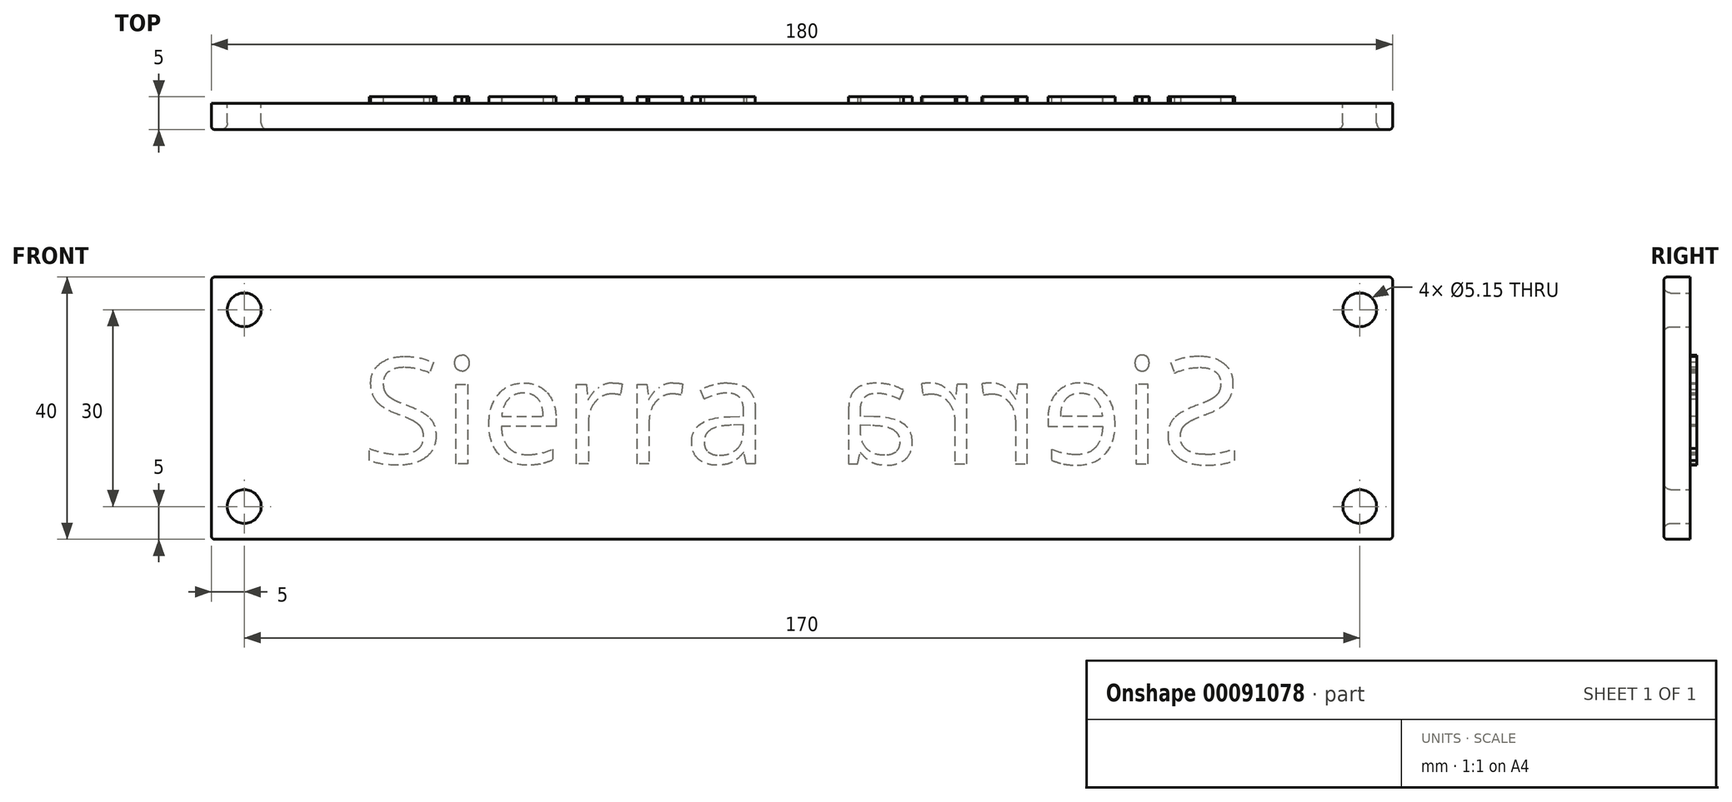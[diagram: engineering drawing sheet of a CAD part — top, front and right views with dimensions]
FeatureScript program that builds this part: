
annotation { "Feature Type Name" : "Feature", "Feature Type Description" : "" }
export const myFeature = defineFeature(function(context is Context, id is Id, definition is map)
    precondition{}
    {
        {
            var Q0;
            Q0=qCreatedBy(makeId("Front.planeOp"),FACE);
            var sketch = newSketch(context, id + "F0", { "sketchPlane" : qUnion([Q0])});
            skLineSegment(sketch, "E0.bottom", {"start": v(-90, -20) * mm, "end": v(90, -20) * mm});
            skLineSegment(sketch, "E0.top", {"start": v(-90, 20) * mm, "end": v(90, 20) * mm});
            skLineSegment(sketch, "E0.left", {"start": v(-90, -20) * mm, "end": v(-90, 20) * mm});
            skLineSegment(sketch, "E0.right", {"start": v(90, -20) * mm, "end": v(90, 20) * mm});
            skPoint(sketch, "E0.middle", {"position": v(0, 0) * mm});
            skCircle(sketch, "E1", {"center": v(-85, 15) * mm, "radius": 2.58 * mm});
            skPoint(sketch, "E2.start.orphan", {"position": v(-90, 0) * mm});
            skPoint(sketch, "E3.orphan", {"position": v(0, 20) * mm});
            skPoint(sketch, "E4.end.orphan", {"position": v(0, -20) * mm});
            skLineSegment(sketch, "E5", {"start": v(-90, 0) * mm, "end": v(0, 0) * mm, "construction": true});
            skLineSegment(sketch, "E6", {"start": v(0, 20) * mm, "end": v(0, -20) * mm, "construction": true});
            skCircle(sketch, "E7.MirrorC", {"center": v(-85, -15) * mm, "radius": 2.58 * mm});
            skCircle(sketch, "E8.MirrorC", {"center": v(85, 15) * mm, "radius": 2.58 * mm});
            skCircle(sketch, "E9.MirrorC", {"center": v(85, -15) * mm, "radius": 2.58 * mm});
            skSolve(sketch);
        }
        {
            var Q0;
            Q0=makeQuery(id+"F0.imprint","IMPRINT",FACE,{"disambiguationData":[TD([[makeQuery(id+"F0.imprint","IMPRINT",EDGE,{"derivedFrom":sQuery(id+"F0.wireOp",EDGE,"E0.bottom")}),1.0]])]});
            extrude(context, id + "F1", {"entities" : qUnion([Q0]), "depth" : 4 * mm});
        }
        {
            var Q0;
            Q0=makeQuery(id+"F1.opExtrude","CAP_EDGE",EDGE,{"disambiguationData":[OSD([sQuery(id+"F0.wireOp",EDGE,"E1")])],"isStart":false});
            var Q1;
            Q1=makeQuery(id+"F1.opExtrude","CAP_EDGE",EDGE,{"disambiguationData":[OSD([sQuery(id+"F0.wireOp",EDGE,"f5b72a5b-8583-449a-bdbf-9ac5a681e1fd0.MirrorC")])],"isStart":false});
            var Q2;
            Q2=makeQuery(id+"F1.opExtrude","CAP_EDGE",EDGE,{"disambiguationData":[OSD([sQuery(id+"F0.wireOp",EDGE,"2623e306-60f4-4522-aa65-1e3e8c2cf5b60.MirrorC")])],"isStart":false});
            var Q3;
            Q3=makeQuery(id+"F1.opExtrude","CAP_EDGE",EDGE,{"disambiguationData":[OSD([sQuery(id+"F0.wireOp",EDGE,"be81a34d-1d50-4ce7-a7a8-4484a1701fac0.MirrorC")])],"isStart":false});
            var Q4;
            Q4=makeQuery(id+"F1.opExtrude","CAP_EDGE",EDGE,{"disambiguationData":[OSD([sQuery(id+"F0.wireOp",EDGE,"E7.MirrorC")])],"isStart":false});
            var Q5;
            Q5=makeQuery(id+"F1.opExtrude","CAP_EDGE",EDGE,{"disambiguationData":[OSD([sQuery(id+"F0.wireOp",EDGE,"E8.MirrorC")])],"isStart":false});
            var Q6;
            Q6=makeQuery(id+"F1.opExtrude","CAP_EDGE",EDGE,{"disambiguationData":[OSD([sQuery(id+"F0.wireOp",EDGE,"E9.MirrorC")])],"isStart":false});
            fillet(context, id + "F2", {"entities" : qUnion([Q0, Q1, Q2, Q3, Q4, Q5, Q6]), "radius" : 1 * mm, "tangentPropagation" : true, "allowEdgeOverflow" : false});
        }
        {
            var Q0;
            Q0=makeQuery(id+"F1.opExtrude","CAP_EDGE",EDGE,{"disambiguationData":[OSD([sQuery(id+"F0.wireOp",EDGE,"E0.top")])],"isStart":false});
            var Q1;
            Q1=makeQuery(id+"F1.opExtrude","CAP_EDGE",EDGE,{"disambiguationData":[OSD([sQuery(id+"F0.wireOp",EDGE,"E0.left")])],"isStart":false});
            var Q2;
            Q2=makeQuery(id+"F1.opExtrude","CAP_EDGE",EDGE,{"disambiguationData":[OSD([sQuery(id+"F0.wireOp",EDGE,"E0.bottom")])],"isStart":false});
            var Q3;
            Q3=makeQuery(id+"F1.opExtrude","CAP_EDGE",EDGE,{"disambiguationData":[OSD([sQuery(id+"F0.wireOp",EDGE,"E0.right")])],"isStart":false});
            var Q4;
            Q4=makeQuery(id+"F1.opExtrude","SWEPT_EDGE",EDGE,{"disambiguationData":[OSD([sQuery(id+"F0.wireOp",EDGE,"E0.top"),sQuery(id+"F0.wireOp",EDGE,"E0.left")])]});
            var Q5;
            Q5=makeQuery(id+"F1.opExtrude","SWEPT_EDGE",EDGE,{"disambiguationData":[OSD([sQuery(id+"F0.wireOp",EDGE,"E0.bottom"),sQuery(id+"F0.wireOp",EDGE,"E0.left")])]});
            var Q6;
            Q6=makeQuery(id+"F1.opExtrude","SWEPT_EDGE",EDGE,{"disambiguationData":[OSD([sQuery(id+"F0.wireOp",EDGE,"E0.top"),sQuery(id+"F0.wireOp",EDGE,"E0.right")])]});
            var Q7;
            Q7=makeQuery(id+"F1.opExtrude","SWEPT_EDGE",EDGE,{"disambiguationData":[OSD([sQuery(id+"F0.wireOp",EDGE,"E0.bottom"),sQuery(id+"F0.wireOp",EDGE,"E0.right")])]});
            fillet(context, id + "F3", {"entities" : qUnion([Q0, Q1, Q2, Q3, Q4, Q5, Q6, Q7]), "radius" : .5 * mm, "tangentPropagation" : true, "allowEdgeOverflow" : false});
        }
        {
            var Q0;
            Q0=makeQuery(id+"F1.opExtrude","CAP_FACE",FACE,{"disambiguationData":[OSD([sQuery(id+"F0.wireOp",EDGE,"E0.bottom"),sQuery(id+"F0.wireOp",EDGE,"E0.top"),sQuery(id+"F0.wireOp",EDGE,"E0.left"),sQuery(id+"F0.wireOp",EDGE,"E0.right"),sQuery(id+"F0.wireOp",EDGE,"E1"),sQuery(id+"F0.wireOp",EDGE,"E7.MirrorC"),sQuery(id+"F0.wireOp",EDGE,"E8.MirrorC"),sQuery(id+"F0.wireOp",EDGE,"E9.MirrorC")])],"isStart":true});
            var sketch = newSketch(context, id + "F4", { "sketchPlane" : qUnion([Q0])});
            skText(sketch, "E10", { "text": "Sierra\n", "fontName": "OpenSans-Regular.ttf"});
            skLineSegment(sketch, "E11", {"start": v(0, 20) * mm, "end": v(0, -20) * mm, "construction": true});
            const initialGuessF4  = {"E10": [-0.0671, -0.00847, 1, 0, 0.01627]};
            skSetInitialGuess(sketch, initialGuessF4);
            skSolve(sketch);
        }
        {
            var Q0;
            Q0=qSketchRegion(id+"F4",true);
            extrude(context, id + "F5", {"entities" : qUnion([Q0]), "operationType" : NewBodyOperationType.ADD, "depth" : 1 * mm});
        }
        {
            var Q0;
            Q0=makeQuery(id+"F1.opExtrude","SWEPT_BODY",BODY,{"disambiguationData":[OSD([sQuery(id+"F0.wireOp",EDGE,"E0.bottom"),sQuery(id+"F0.wireOp",EDGE,"E0.top"),sQuery(id+"F0.wireOp",EDGE,"E0.left"),sQuery(id+"F0.wireOp",EDGE,"E0.right"),sQuery(id+"F0.wireOp",EDGE,"E1"),sQuery(id+"F0.wireOp",EDGE,"E7.MirrorC"),sQuery(id+"F0.wireOp",EDGE,"E8.MirrorC"),sQuery(id+"F0.wireOp",EDGE,"E9.MirrorC")])]});
            var Q1;
            Q1=makeQuery(id+"F5.opExtrude","SWEPT_FACE",FACE,{"disambiguationData":[OSD([sQuery(id+"F4.wireOp",EDGE,"E10.sketch_text.stroke-94")])]});
            var Q2;
            Q2=makeQuery(id+"F5.opExtrude","SWEPT_FACE",FACE,{"disambiguationData":[OSD([sQuery(id+"F4.wireOp",EDGE,"E10.sketch_text.stroke-169")])]});
            var Q3;
            Q3=makeQuery(id+"F5.opExtrude","SWEPT_FACE",FACE,{"disambiguationData":[OSD([sQuery(id+"F4.wireOp",EDGE,"E10.sketch_text.stroke-185")])]});
            var Q4;
            Q4=makeQuery(id+"F5.opExtrude","SWEPT_FACE",FACE,{"disambiguationData":[OSD([sQuery(id+"F4.wireOp",EDGE,"E10.sketch_text.stroke-125")])]});
            var Q5;
            Q5=makeQuery(id+"F5.opExtrude","SWEPT_FACE",FACE,{"disambiguationData":[OSD([sQuery(id+"F4.wireOp",EDGE,"E10.sketch_text.stroke-155")])]});
            var Q6;
            Q6=makeQuery(id+"F5.opExtrude","SWEPT_FACE",FACE,{"disambiguationData":[OSD([sQuery(id+"F4.wireOp",EDGE,"E10.sketch_text.stroke-65")])]});
            var Q7;
            Q7=makeQuery(id+"F5.opExtrude","SWEPT_FACE",FACE,{"disambiguationData":[OSD([sQuery(id+"F4.wireOp",EDGE,"E10.sketch_text.stroke-81")])]});
            var Q8;
            Q8=makeQuery(id+"F5.opExtrude","SWEPT_FACE",FACE,{"disambiguationData":[OSD([sQuery(id+"F4.wireOp",EDGE,"E10.sketch_text.stroke-67")])]});
            var Q9;
            Q9=makeQuery(id+"F5.opExtrude","SWEPT_FACE",FACE,{"disambiguationData":[OSD([sQuery(id+"F4.wireOp",EDGE,"E10.sketch_text.stroke-99")])]});
            var Q10;
            Q10=makeQuery(id+"F5.opExtrude","SWEPT_FACE",FACE,{"disambiguationData":[OSD([sQuery(id+"F4.wireOp",EDGE,"E10.sketch_text.stroke-127")])]});
            var Q11;
            Q11=makeQuery(id+"F5.opExtrude","SWEPT_FACE",FACE,{"disambiguationData":[OSD([sQuery(id+"F4.wireOp",EDGE,"E10.sketch_text.stroke-10")])]});
            var Q12;
            Q12=makeQuery(id+"F5.opExtrude","CAP_FACE",FACE,{"disambiguationData":[OSD([sQuery(id+"F4.wireOp",EDGE,"E10.sketch_text.stroke-9"),sQuery(id+"F4.wireOp",EDGE,"E10.sketch_text.stroke-10"),sQuery(id+"F4.wireOp",EDGE,"E10.sketch_text.stroke-11"),sQuery(id+"F4.wireOp",EDGE,"E10.sketch_text.stroke-12")])],"isStart":false});
            var Q13;
            Q13=makeQuery(id+"F5.opExtrude","SWEPT_FACE",FACE,{"disambiguationData":[OSD([sQuery(id+"F4.wireOp",EDGE,"E10.sketch_text.stroke-154")])]});
            var Q14;
            Q14=makeQuery(id+"F5.opExtrude","SWEPT_FACE",FACE,{"disambiguationData":[OSD([sQuery(id+"F4.wireOp",EDGE,"E10.sketch_text.stroke-1")])]});
            var Q15;
            Q15=makeQuery(id+"F5.opExtrude","CAP_FACE",FACE,{"disambiguationData":[OSD([sQuery(id+"F4.wireOp",EDGE,"E10.sketch_text.stroke-124"),sQuery(id+"F4.wireOp",EDGE,"E10.sketch_text.stroke-125"),sQuery(id+"F4.wireOp",EDGE,"E10.sketch_text.stroke-126"),sQuery(id+"F4.wireOp",EDGE,"E10.sketch_text.stroke-127"),sQuery(id+"F4.wireOp",EDGE,"E10.sketch_text.stroke-128"),sQuery(id+"F4.wireOp",EDGE,"E10.sketch_text.stroke-129"),sQuery(id+"F4.wireOp",EDGE,"E10.sketch_text.stroke-130"),sQuery(id+"F4.wireOp",EDGE,"E10.sketch_text.stroke-131"),sQuery(id+"F4.wireOp",EDGE,"E10.sketch_text.stroke-132"),sQuery(id+"F4.wireOp",EDGE,"E10.sketch_text.stroke-133"),sQuery(id+"F4.wireOp",EDGE,"E10.sketch_text.stroke-134"),sQuery(id+"F4.wireOp",EDGE,"E10.sketch_text.stroke-135"),sQuery(id+"F4.wireOp",EDGE,"E10.sketch_text.stroke-136"),sQuery(id+"F4.wireOp",EDGE,"E10.sketch_text.stroke-137"),sQuery(id+"F4.wireOp",EDGE,"E10.sketch_text.stroke-138")])],"isStart":false});
            var Q16;
            Q16=makeQuery(id+"F5.opExtrude","CAP_FACE",FACE,{"disambiguationData":[OSD([sQuery(id+"F4.wireOp",EDGE,"E10.sketch_text.stroke-34"),sQuery(id+"F4.wireOp",EDGE,"E10.sketch_text.stroke-35"),sQuery(id+"F4.wireOp",EDGE,"E10.sketch_text.stroke-36"),sQuery(id+"F4.wireOp",EDGE,"E10.sketch_text.stroke-37"),sQuery(id+"F4.wireOp",EDGE,"E10.sketch_text.stroke-38"),sQuery(id+"F4.wireOp",EDGE,"E10.sketch_text.stroke-39"),sQuery(id+"F4.wireOp",EDGE,"E10.sketch_text.stroke-40"),sQuery(id+"F4.wireOp",EDGE,"E10.sketch_text.stroke-41"),sQuery(id+"F4.wireOp",EDGE,"E10.sketch_text.stroke-42"),sQuery(id+"F4.wireOp",EDGE,"E10.sketch_text.stroke-43"),sQuery(id+"F4.wireOp",EDGE,"E10.sketch_text.stroke-44"),sQuery(id+"F4.wireOp",EDGE,"E10.sketch_text.stroke-45"),sQuery(id+"F4.wireOp",EDGE,"E10.sketch_text.stroke-46"),sQuery(id+"F4.wireOp",EDGE,"E10.sketch_text.stroke-47"),sQuery(id+"F4.wireOp",EDGE,"E10.sketch_text.stroke-48"),sQuery(id+"F4.wireOp",EDGE,"E10.sketch_text.stroke-49"),sQuery(id+"F4.wireOp",EDGE,"E10.sketch_text.stroke-50"),sQuery(id+"F4.wireOp",EDGE,"E10.sketch_text.stroke-51"),sQuery(id+"F4.wireOp",EDGE,"E10.sketch_text.stroke-52"),sQuery(id+"F4.wireOp",EDGE,"E10.sketch_text.stroke-53"),sQuery(id+"F4.wireOp",EDGE,"E10.sketch_text.stroke-54"),sQuery(id+"F4.wireOp",EDGE,"E10.sketch_text.stroke-55"),sQuery(id+"F4.wireOp",EDGE,"E10.sketch_text.stroke-56"),sQuery(id+"F4.wireOp",EDGE,"E10.sketch_text.stroke-57"),sQuery(id+"F4.wireOp",EDGE,"E10.sketch_text.stroke-58"),sQuery(id+"F4.wireOp",EDGE,"E10.sketch_text.stroke-59"),sQuery(id+"F4.wireOp",EDGE,"E10.sketch_text.stroke-60")])],"isStart":false});
            var Q17;
            Q17=makeQuery(id+"F5.opExtrude","SWEPT_FACE",FACE,{"disambiguationData":[OSD([sQuery(id+"F4.wireOp",EDGE,"E10.sketch_text.stroke-50")])]});
            var Q18;
            Q18=makeQuery(id+"F5.opExtrude","SWEPT_FACE",FACE,{"disambiguationData":[OSD([sQuery(id+"F4.wireOp",EDGE,"E10.sketch_text.stroke-2")])]});
            var Q19;
            Q19=makeQuery(id+"F5.opExtrude","SWEPT_FACE",FACE,{"disambiguationData":[OSD([sQuery(id+"F4.wireOp",EDGE,"E10.sketch_text.stroke-3")])]});
            var Q20;
            Q20=makeQuery(id+"F5.opExtrude","SWEPT_FACE",FACE,{"disambiguationData":[OSD([sQuery(id+"F4.wireOp",EDGE,"E10.sketch_text.stroke-5")])]});
            var Q21;
            Q21=makeQuery(id+"F5.opExtrude","SWEPT_FACE",FACE,{"disambiguationData":[OSD([sQuery(id+"F4.wireOp",EDGE,"E10.sketch_text.stroke-8")])]});
            var Q22;
            Q22=makeQuery(id+"F5.opExtrude","SWEPT_FACE",FACE,{"disambiguationData":[OSD([sQuery(id+"F4.wireOp",EDGE,"E10.sketch_text.stroke-98")])]});
            var Q23;
            Q23=makeQuery(id+"F5.opExtrude","SWEPT_FACE",FACE,{"disambiguationData":[OSD([sQuery(id+"F4.wireOp",EDGE,"E10.sketch_text.stroke-66")])]});
            var Q24;
            Q24=makeQuery(id+"F5.opExtrude","SWEPT_FACE",FACE,{"disambiguationData":[OSD([sQuery(id+"F4.wireOp",EDGE,"E10.sketch_text.stroke-153")])]});
            var Q25;
            Q25=makeQuery(id+"F5.opExtrude","SWEPT_FACE",FACE,{"disambiguationData":[OSD([sQuery(id+"F4.wireOp",EDGE,"E10.sketch_text.stroke-126")])]});
            var Q26;
            Q26=makeQuery(id+"F5.opExtrude","SWEPT_FACE",FACE,{"disambiguationData":[OSD([sQuery(id+"F4.wireOp",EDGE,"E10.sketch_text.stroke-183")])]});
            var Q27;
            Q27=makeQuery(id+"F5.opExtrude","SWEPT_FACE",FACE,{"disambiguationData":[OSD([sQuery(id+"F4.wireOp",EDGE,"E10.sketch_text.stroke-109")])]});
            var Q28;
            Q28=makeQuery(id+"F5.opExtrude","SWEPT_FACE",FACE,{"disambiguationData":[OSD([sQuery(id+"F4.wireOp",EDGE,"E10.sketch_text.stroke-186")])]});
            var Q29;
            Q29=makeQuery(id+"F5.opExtrude","SWEPT_FACE",FACE,{"disambiguationData":[OSD([sQuery(id+"F4.wireOp",EDGE,"E10.sketch_text.stroke-79")])]});
            var Q30;
            Q30=makeQuery(id+"F5.opExtrude","SWEPT_FACE",FACE,{"disambiguationData":[OSD([sQuery(id+"F4.wireOp",EDGE,"E10.sketch_text.stroke-110")])]});
            var Q31;
            Q31=makeQuery(id+"F5.opExtrude","SWEPT_FACE",FACE,{"disambiguationData":[OSD([sQuery(id+"F4.wireOp",EDGE,"E10.sketch_text.stroke-38")])]});
            var Q32;
            Q32=makeQuery(id+"F5.opExtrude","SWEPT_FACE",FACE,{"disambiguationData":[OSD([sQuery(id+"F4.wireOp",EDGE,"E10.sketch_text.stroke-24")])]});
            var Q33;
            Q33=makeQuery(id+"F5.opExtrude","SWEPT_FACE",FACE,{"disambiguationData":[OSD([sQuery(id+"F4.wireOp",EDGE,"E10.sketch_text.stroke-12")])]});
            var Q34;
            Q34=makeQuery(id+"F5.opExtrude","SWEPT_FACE",FACE,{"disambiguationData":[OSD([sQuery(id+"F4.wireOp",EDGE,"E10.sketch_text.stroke-100")])]});
            var Q35;
            Q35=makeQuery(id+"F5.opExtrude","SWEPT_FACE",FACE,{"disambiguationData":[OSD([sQuery(id+"F4.wireOp",EDGE,"E10.sketch_text.stroke-158")])]});
            var Q36;
            Q36=makeQuery(id+"F5.opExtrude","SWEPT_FACE",FACE,{"disambiguationData":[OSD([sQuery(id+"F4.wireOp",EDGE,"E10.sketch_text.stroke-142")])]});
            var Q37;
            Q37=makeQuery(id+"F5.opExtrude","SWEPT_FACE",FACE,{"disambiguationData":[OSD([sQuery(id+"F4.wireOp",EDGE,"E10.sketch_text.stroke-54")])]});
            var Q38;
            Q38=makeQuery(id+"F5.opExtrude","SWEPT_FACE",FACE,{"disambiguationData":[OSD([sQuery(id+"F4.wireOp",EDGE,"E10.sketch_text.stroke-25")])]});
            var Q39;
            Q39=makeQuery(id+"F5.opExtrude","SWEPT_FACE",FACE,{"disambiguationData":[OSD([sQuery(id+"F4.wireOp",EDGE,"E10.sketch_text.stroke-101")])]});
            var Q40;
            Q40=makeQuery(id+"F5.opExtrude","SWEPT_FACE",FACE,{"disambiguationData":[OSD([sQuery(id+"F4.wireOp",EDGE,"E10.sketch_text.stroke-69")])]});
            var Q41;
            Q41=makeQuery(id+"F5.opExtrude","SWEPT_FACE",FACE,{"disambiguationData":[OSD([sQuery(id+"F4.wireOp",EDGE,"E10.sketch_text.stroke-159")])]});
            var Q42;
            Q42=makeQuery(id+"F5.opExtrude","SWEPT_FACE",FACE,{"disambiguationData":[OSD([sQuery(id+"F4.wireOp",EDGE,"E10.sketch_text.stroke-85")])]});
            var Q43;
            Q43=makeQuery(id+"F5.opExtrude","SWEPT_FACE",FACE,{"disambiguationData":[OSD([sQuery(id+"F4.wireOp",EDGE,"E10.sketch_text.stroke-173")])]});
            var Q44;
            Q44=makeQuery(id+"F5.opExtrude","SWEPT_FACE",FACE,{"disambiguationData":[OSD([sQuery(id+"F4.wireOp",EDGE,"E10.sketch_text.stroke-40")])]});
            var Q45;
            Q45=makeQuery(id+"F5.opExtrude","SWEPT_FACE",FACE,{"disambiguationData":[OSD([sQuery(id+"F4.wireOp",EDGE,"E10.sketch_text.stroke-102")])]});
            var Q46;
            Q46=makeQuery(id+"F5.opExtrude","SWEPT_FACE",FACE,{"disambiguationData":[OSD([sQuery(id+"F4.wireOp",EDGE,"E10.sketch_text.stroke-86")])]});
            var Q47;
            Q47=makeQuery(id+"F5.opExtrude","SWEPT_FACE",FACE,{"disambiguationData":[OSD([sQuery(id+"F4.wireOp",EDGE,"E10.sketch_text.stroke-130")])]});
            var Q48;
            Q48=makeQuery(id+"F5.opExtrude","SWEPT_FACE",FACE,{"disambiguationData":[OSD([sQuery(id+"F4.wireOp",EDGE,"E10.sketch_text.stroke-103")])]});
            var Q49;
            Q49=makeQuery(id+"F5.opExtrude","SWEPT_FACE",FACE,{"disambiguationData":[OSD([sQuery(id+"F4.wireOp",EDGE,"E10.sketch_text.stroke-87")])]});
            var Q50;
            Q50=makeQuery(id+"F5.opExtrude","SWEPT_FACE",FACE,{"disambiguationData":[OSD([sQuery(id+"F4.wireOp",EDGE,"E10.sketch_text.stroke-145")])]});
            var Q51;
            Q51=makeQuery(id+"F5.opExtrude","SWEPT_FACE",FACE,{"disambiguationData":[OSD([sQuery(id+"F4.wireOp",EDGE,"E10.sketch_text.stroke-131")])]});
            var Q52;
            Q52=makeQuery(id+"F5.opExtrude","SWEPT_FACE",FACE,{"disambiguationData":[OSD([sQuery(id+"F4.wireOp",EDGE,"E10.sketch_text.stroke-28")])]});
            var Q53;
            Q53=makeQuery(id+"F5.opExtrude","SWEPT_FACE",FACE,{"disambiguationData":[OSD([sQuery(id+"F4.wireOp",EDGE,"E10.sketch_text.stroke-14")])]});
            var Q54;
            Q54=makeQuery(id+"F5.opExtrude","SWEPT_FACE",FACE,{"disambiguationData":[OSD([sQuery(id+"F4.wireOp",EDGE,"E10.sketch_text.stroke-88")])]});
            var Q55;
            Q55=makeQuery(id+"F5.opExtrude","SWEPT_FACE",FACE,{"disambiguationData":[OSD([sQuery(id+"F4.wireOp",EDGE,"E10.sketch_text.stroke-162")])]});
            var Q56;
            Q56=makeQuery(id+"F5.opExtrude","SWEPT_FACE",FACE,{"disambiguationData":[OSD([sQuery(id+"F4.wireOp",EDGE,"E10.sketch_text.stroke-176")])]});
            var Q57;
            Q57=makeQuery(id+"F5.opExtrude","SWEPT_FACE",FACE,{"disambiguationData":[OSD([sQuery(id+"F4.wireOp",EDGE,"E10.sketch_text.stroke-73")])]});
            var Q58;
            Q58=makeQuery(id+"F5.opExtrude","SWEPT_FACE",FACE,{"disambiguationData":[OSD([sQuery(id+"F4.wireOp",EDGE,"E10.sketch_text.stroke-59")])]});
            var Q59;
            Q59=makeQuery(id+"F5.opExtrude","SWEPT_FACE",FACE,{"disambiguationData":[OSD([sQuery(id+"F4.wireOp",EDGE,"E10.sketch_text.stroke-133")])]});
            var Q60;
            Q60=makeQuery(id+"F5.opExtrude","SWEPT_FACE",FACE,{"disambiguationData":[OSD([sQuery(id+"F4.wireOp",EDGE,"E10.sketch_text.stroke-119")])]});
            var Q61;
            Q61=makeQuery(id+"F5.opExtrude","SWEPT_FACE",FACE,{"disambiguationData":[OSD([sQuery(id+"F4.wireOp",EDGE,"E10.sketch_text.stroke-74")])]});
            var Q62;
            Q62=makeQuery(id+"F5.opExtrude","SWEPT_FACE",FACE,{"disambiguationData":[OSD([sQuery(id+"F4.wireOp",EDGE,"E10.sketch_text.stroke-44")])]});
            var Q63;
            Q63=makeQuery(id+"F5.opExtrude","SWEPT_FACE",FACE,{"disambiguationData":[OSD([sQuery(id+"F4.wireOp",EDGE,"E10.sketch_text.stroke-120")])]});
            var Q64;
            Q64=makeQuery(id+"F5.opExtrude","SWEPT_FACE",FACE,{"disambiguationData":[OSD([sQuery(id+"F4.wireOp",EDGE,"E10.sketch_text.stroke-90")])]});
            var Q65;
            Q65=makeQuery(id+"F5.opExtrude","SWEPT_FACE",FACE,{"disambiguationData":[OSD([sQuery(id+"F4.wireOp",EDGE,"E10.sketch_text.stroke-178")])]});
            var Q66;
            Q66=makeQuery(id+"F5.opExtrude","SWEPT_FACE",FACE,{"disambiguationData":[OSD([sQuery(id+"F4.wireOp",EDGE,"E10.sketch_text.stroke-45")])]});
            var Q67;
            Q67=makeQuery(id+"F5.opExtrude","SWEPT_FACE",FACE,{"disambiguationData":[OSD([sQuery(id+"F4.wireOp",EDGE,"E10.sketch_text.stroke-31")])]});
            var Q68;
            Q68=makeQuery(id+"F5.opExtrude","SWEPT_FACE",FACE,{"disambiguationData":[OSD([sQuery(id+"F4.wireOp",EDGE,"E10.sketch_text.stroke-135")])]});
            var Q69;
            Q69=makeQuery(id+"F5.opExtrude","SWEPT_FACE",FACE,{"disambiguationData":[OSD([sQuery(id+"F4.wireOp",EDGE,"E10.sketch_text.stroke-179")])]});
            var Q70;
            Q70=makeQuery(id+"F5.opExtrude","SWEPT_FACE",FACE,{"disambiguationData":[OSD([sQuery(id+"F4.wireOp",EDGE,"E10.sketch_text.stroke-165")])]});
            var Q71;
            Q71=makeQuery(id+"F5.opExtrude","SWEPT_FACE",FACE,{"disambiguationData":[OSD([sQuery(id+"F4.wireOp",EDGE,"E10.sketch_text.stroke-149")])]});
            var Q72;
            Q72=makeQuery(id+"F5.opExtrude","SWEPT_FACE",FACE,{"disambiguationData":[OSD([sQuery(id+"F4.wireOp",EDGE,"E10.sketch_text.stroke-136")])]});
            var Q73;
            Q73=makeQuery(id+"F5.opExtrude","SWEPT_FACE",FACE,{"disambiguationData":[OSD([sQuery(id+"F4.wireOp",EDGE,"E10.sketch_text.stroke-122")])]});
            var Q74;
            Q74=makeQuery(id+"F5.opExtrude","SWEPT_FACE",FACE,{"disambiguationData":[OSD([sQuery(id+"F4.wireOp",EDGE,"E10.sketch_text.stroke-106")])]});
            var Q75;
            Q75=makeQuery(id+"F5.opExtrude","SWEPT_FACE",FACE,{"disambiguationData":[OSD([sQuery(id+"F4.wireOp",EDGE,"E10.sketch_text.stroke-180")])]});
            var Q76;
            Q76=makeQuery(id+"F5.opExtrude","SWEPT_FACE",FACE,{"disambiguationData":[OSD([sQuery(id+"F4.wireOp",EDGE,"E10.sketch_text.stroke-166")])]});
            var Q77;
            Q77=makeQuery(id+"F5.opExtrude","SWEPT_FACE",FACE,{"disambiguationData":[OSD([sQuery(id+"F4.wireOp",EDGE,"E10.sketch_text.stroke-150")])]});
            var Q78;
            Q78=makeQuery(id+"F5.opExtrude","SWEPT_FACE",FACE,{"disambiguationData":[OSD([sQuery(id+"F4.wireOp",EDGE,"E10.sketch_text.stroke-76")])]});
            var Q79;
            Q79=makeQuery(id+"F5.opExtrude","SWEPT_FACE",FACE,{"disambiguationData":[OSD([sQuery(id+"F4.wireOp",EDGE,"E10.sketch_text.stroke-32")])]});
            var Q80;
            Q80=makeQuery(id+"F5.opExtrude","SWEPT_FACE",FACE,{"disambiguationData":[OSD([sQuery(id+"F4.wireOp",EDGE,"E10.sketch_text.stroke-181")])]});
            var Q81;
            Q81=makeQuery(id+"F5.opExtrude","SWEPT_FACE",FACE,{"disambiguationData":[OSD([sQuery(id+"F4.wireOp",EDGE,"E10.sketch_text.stroke-47")])]});
            var Q82;
            Q82=makeQuery(id+"F5.opExtrude","SWEPT_FACE",FACE,{"disambiguationData":[OSD([sQuery(id+"F4.wireOp",EDGE,"E10.sketch_text.stroke-123")])]});
            var Q83;
            Q83=makeQuery(id+"F5.opExtrude","SWEPT_FACE",FACE,{"disambiguationData":[OSD([sQuery(id+"F4.wireOp",EDGE,"E10.sketch_text.stroke-107")])]});
            var Q84;
            Q84=makeQuery(id+"F5.opExtrude","SWEPT_FACE",FACE,{"disambiguationData":[OSD([sQuery(id+"F4.wireOp",EDGE,"E10.sketch_text.stroke-48")])]});
            var Q85;
            Q85=makeQuery(id+"F5.opExtrude","SWEPT_FACE",FACE,{"disambiguationData":[OSD([sQuery(id+"F4.wireOp",EDGE,"E10.sketch_text.stroke-124")])]});
            var Q86;
            Q86=makeQuery(id+"F5.opExtrude","SWEPT_FACE",FACE,{"disambiguationData":[OSD([sQuery(id+"F4.wireOp",EDGE,"E10.sketch_text.stroke-108")])]});
            var Q87;
            Q87=makeQuery(id+"F5.opExtrude","CAP_FACE",FACE,{"disambiguationData":[OSD([sQuery(id+"F4.wireOp",EDGE,"E10.sketch_text.stroke-139"),sQuery(id+"F4.wireOp",EDGE,"E10.sketch_text.stroke-140"),sQuery(id+"F4.wireOp",EDGE,"E10.sketch_text.stroke-141"),sQuery(id+"F4.wireOp",EDGE,"E10.sketch_text.stroke-142"),sQuery(id+"F4.wireOp",EDGE,"E10.sketch_text.stroke-143"),sQuery(id+"F4.wireOp",EDGE,"E10.sketch_text.stroke-144"),sQuery(id+"F4.wireOp",EDGE,"E10.sketch_text.stroke-145"),sQuery(id+"F4.wireOp",EDGE,"E10.sketch_text.stroke-146"),sQuery(id+"F4.wireOp",EDGE,"E10.sketch_text.stroke-147"),sQuery(id+"F4.wireOp",EDGE,"E10.sketch_text.stroke-148"),sQuery(id+"F4.wireOp",EDGE,"E10.sketch_text.stroke-149"),sQuery(id+"F4.wireOp",EDGE,"E10.sketch_text.stroke-150"),sQuery(id+"F4.wireOp",EDGE,"E10.sketch_text.stroke-151"),sQuery(id+"F4.wireOp",EDGE,"E10.sketch_text.stroke-152"),sQuery(id+"F4.wireOp",EDGE,"E10.sketch_text.stroke-153"),sQuery(id+"F4.wireOp",EDGE,"E10.sketch_text.stroke-154"),sQuery(id+"F4.wireOp",EDGE,"E10.sketch_text.stroke-155"),sQuery(id+"F4.wireOp",EDGE,"E10.sketch_text.stroke-156"),sQuery(id+"F4.wireOp",EDGE,"E10.sketch_text.stroke-157"),sQuery(id+"F4.wireOp",EDGE,"E10.sketch_text.stroke-158"),sQuery(id+"F4.wireOp",EDGE,"E10.sketch_text.stroke-159"),sQuery(id+"F4.wireOp",EDGE,"E10.sketch_text.stroke-160"),sQuery(id+"F4.wireOp",EDGE,"E10.sketch_text.stroke-161"),sQuery(id+"F4.wireOp",EDGE,"E10.sketch_text.stroke-162"),sQuery(id+"F4.wireOp",EDGE,"E10.sketch_text.stroke-163"),sQuery(id+"F4.wireOp",EDGE,"E10.sketch_text.stroke-164"),sQuery(id+"F4.wireOp",EDGE,"E10.sketch_text.stroke-165")])],"isStart":false});
            var Q88;
            Q88=makeQuery(id+"F5.opExtrude","CAP_FACE",FACE,{"disambiguationData":[OSD([sQuery(id+"F4.wireOp",EDGE,"E10.sketch_text.stroke-21"),sQuery(id+"F4.wireOp",EDGE,"E10.sketch_text.stroke-22"),sQuery(id+"F4.wireOp",EDGE,"E10.sketch_text.stroke-23"),sQuery(id+"F4.wireOp",EDGE,"E10.sketch_text.stroke-24"),sQuery(id+"F4.wireOp",EDGE,"E10.sketch_text.stroke-25"),sQuery(id+"F4.wireOp",EDGE,"E10.sketch_text.stroke-26"),sQuery(id+"F4.wireOp",EDGE,"E10.sketch_text.stroke-27"),sQuery(id+"F4.wireOp",EDGE,"E10.sketch_text.stroke-28"),sQuery(id+"F4.wireOp",EDGE,"E10.sketch_text.stroke-29"),sQuery(id+"F4.wireOp",EDGE,"E10.sketch_text.stroke-30"),sQuery(id+"F4.wireOp",EDGE,"E10.sketch_text.stroke-31"),sQuery(id+"F4.wireOp",EDGE,"E10.sketch_text.stroke-32"),sQuery(id+"F4.wireOp",EDGE,"E10.sketch_text.stroke-33")])],"isStart":false});
            var Q89;
            Q89=makeQuery(id+"F5.opExtrude","SWEPT_FACE",FACE,{"disambiguationData":[OSD([sQuery(id+"F4.wireOp",EDGE,"E10.sketch_text.stroke-113")])]});
            var Q90;
            Q90=makeQuery(id+"F5.opExtrude","SWEPT_FACE",FACE,{"disambiguationData":[OSD([sQuery(id+"F4.wireOp",EDGE,"E10.sketch_text.stroke-37")])]});
            var Q91;
            Q91=makeQuery(id+"F5.opExtrude","SWEPT_FACE",FACE,{"disambiguationData":[OSD([sQuery(id+"F4.wireOp",EDGE,"E10.sketch_text.stroke-187")])]});
            var Q92;
            Q92=makeQuery(id+"F5.opExtrude","SWEPT_FACE",FACE,{"disambiguationData":[OSD([sQuery(id+"F4.wireOp",EDGE,"E10.sketch_text.stroke-0")])]});
            var Q93;
            Q93=makeQuery(id+"F5.opExtrude","SWEPT_FACE",FACE,{"disambiguationData":[OSD([sQuery(id+"F4.wireOp",EDGE,"E10.sketch_text.stroke-4")])]});
            var Q94;
            Q94=makeQuery(id+"F5.opExtrude","SWEPT_FACE",FACE,{"disambiguationData":[OSD([sQuery(id+"F4.wireOp",EDGE,"E10.sketch_text.stroke-82")])]});
            var Q95;
            Q95=makeQuery(id+"F5.opExtrude","SWEPT_FACE",FACE,{"disambiguationData":[OSD([sQuery(id+"F4.wireOp",EDGE,"E10.sketch_text.stroke-52")])]});
            var Q96;
            Q96=makeQuery(id+"F5.opExtrude","SWEPT_FACE",FACE,{"disambiguationData":[OSD([sQuery(id+"F4.wireOp",EDGE,"E10.sketch_text.stroke-49")])]});
            var Q97;
            Q97=makeQuery(id+"F5.opExtrude","SWEPT_FACE",FACE,{"disambiguationData":[OSD([sQuery(id+"F4.wireOp",EDGE,"E10.sketch_text.stroke-63")])]});
            var Q98;
            Q98=makeQuery(id+"F5.opExtrude","SWEPT_FACE",FACE,{"disambiguationData":[OSD([sQuery(id+"F4.wireOp",EDGE,"E10.sketch_text.stroke-21")])]});
            var Q99;
            Q99=makeQuery(id+"F5.opExtrude","SWEPT_FACE",FACE,{"disambiguationData":[OSD([sQuery(id+"F4.wireOp",EDGE,"E10.sketch_text.stroke-128")])]});
            var Q100;
            Q100=makeQuery(id+"F5.opExtrude","SWEPT_FACE",FACE,{"disambiguationData":[OSD([sQuery(id+"F4.wireOp",EDGE,"E10.sketch_text.stroke-55")])]});
            var Q101;
            Q101=makeQuery(id+"F5.opExtrude","SWEPT_FACE",FACE,{"disambiguationData":[OSD([sQuery(id+"F4.wireOp",EDGE,"E10.sketch_text.stroke-26")])]});
            var Q102;
            Q102=makeQuery(id+"F5.opExtrude","SWEPT_FACE",FACE,{"disambiguationData":[OSD([sQuery(id+"F4.wireOp",EDGE,"E10.sketch_text.stroke-174")])]});
            var Q103;
            Q103=makeQuery(id+"F5.opExtrude","SWEPT_FACE",FACE,{"disambiguationData":[OSD([sQuery(id+"F4.wireOp",EDGE,"E10.sketch_text.stroke-104")])]});
            var Q104;
            Q104=makeQuery(id+"F5.opExtrude","SWEPT_FACE",FACE,{"disambiguationData":[OSD([sQuery(id+"F4.wireOp",EDGE,"E10.sketch_text.stroke-72")])]});
            var Q105;
            Q105=makeQuery(id+"F5.opExtrude","SWEPT_FACE",FACE,{"disambiguationData":[OSD([sQuery(id+"F4.wireOp",EDGE,"E10.sketch_text.stroke-132")])]});
            var Q106;
            Q106=makeQuery(id+"F5.opExtrude","SWEPT_FACE",FACE,{"disambiguationData":[OSD([sQuery(id+"F4.wireOp",EDGE,"E10.sketch_text.stroke-43")])]});
            var Q107;
            Q107=makeQuery(id+"F5.opExtrude","SWEPT_FACE",FACE,{"disambiguationData":[OSD([sQuery(id+"F4.wireOp",EDGE,"E10.sketch_text.stroke-15")])]});
            var Q108;
            Q108=makeQuery(id+"F5.opExtrude","SWEPT_FACE",FACE,{"disambiguationData":[OSD([sQuery(id+"F4.wireOp",EDGE,"E10.sketch_text.stroke-89")])]});
            var Q109;
            Q109=makeQuery(id+"F5.opExtrude","SWEPT_FACE",FACE,{"disambiguationData":[OSD([sQuery(id+"F4.wireOp",EDGE,"E10.sketch_text.stroke-163")])]});
            var Q110;
            Q110=makeQuery(id+"F5.opExtrude","SWEPT_FACE",FACE,{"disambiguationData":[OSD([sQuery(id+"F4.wireOp",EDGE,"E10.sketch_text.stroke-30")])]});
            var Q111;
            Q111=makeQuery(id+"F5.opExtrude","SWEPT_FACE",FACE,{"disambiguationData":[OSD([sQuery(id+"F4.wireOp",EDGE,"E10.sketch_text.stroke-134")])]});
            var Q112;
            Q112=makeQuery(id+"F5.opExtrude","SWEPT_FACE",FACE,{"disambiguationData":[OSD([sQuery(id+"F4.wireOp",EDGE,"E10.sketch_text.stroke-121")])]});
            var Q113;
            Q113=makeQuery(id+"F5.opExtrude","CAP_FACE",FACE,{"disambiguationData":[OSD([sQuery(id+"F4.wireOp",EDGE,"E10.sketch_text.stroke-105"),sQuery(id+"F4.wireOp",EDGE,"E10.sketch_text.stroke-106"),sQuery(id+"F4.wireOp",EDGE,"E10.sketch_text.stroke-107"),sQuery(id+"F4.wireOp",EDGE,"E10.sketch_text.stroke-108"),sQuery(id+"F4.wireOp",EDGE,"E10.sketch_text.stroke-109"),sQuery(id+"F4.wireOp",EDGE,"E10.sketch_text.stroke-110"),sQuery(id+"F4.wireOp",EDGE,"E10.sketch_text.stroke-111"),sQuery(id+"F4.wireOp",EDGE,"E10.sketch_text.stroke-112"),sQuery(id+"F4.wireOp",EDGE,"E10.sketch_text.stroke-113"),sQuery(id+"F4.wireOp",EDGE,"E10.sketch_text.stroke-114"),sQuery(id+"F4.wireOp",EDGE,"E10.sketch_text.stroke-115"),sQuery(id+"F4.wireOp",EDGE,"E10.sketch_text.stroke-116"),sQuery(id+"F4.wireOp",EDGE,"E10.sketch_text.stroke-117"),sQuery(id+"F4.wireOp",EDGE,"E10.sketch_text.stroke-118"),sQuery(id+"F4.wireOp",EDGE,"E10.sketch_text.stroke-119"),sQuery(id+"F4.wireOp",EDGE,"E10.sketch_text.stroke-120"),sQuery(id+"F4.wireOp",EDGE,"E10.sketch_text.stroke-121"),sQuery(id+"F4.wireOp",EDGE,"E10.sketch_text.stroke-122"),sQuery(id+"F4.wireOp",EDGE,"E10.sketch_text.stroke-123")])],"isStart":false});
            var Q114;
            Q114=makeQuery(id+"F5.opExtrude","SWEPT_FACE",FACE,{"disambiguationData":[OSD([sQuery(id+"F4.wireOp",EDGE,"E10.sketch_text.stroke-92")])]});
            var Q115;
            Q115=makeQuery(id+"F5.opExtrude","SWEPT_FACE",FACE,{"disambiguationData":[OSD([sQuery(id+"F4.wireOp",EDGE,"E10.sketch_text.stroke-46")])]});
            var Q116;
            Q116=makeQuery(id+"F5.opExtrude","CAP_FACE",FACE,{"disambiguationData":[OSD([sQuery(id+"F4.wireOp",EDGE,"E10.sketch_text.stroke-61"),sQuery(id+"F4.wireOp",EDGE,"E10.sketch_text.stroke-62"),sQuery(id+"F4.wireOp",EDGE,"E10.sketch_text.stroke-63"),sQuery(id+"F4.wireOp",EDGE,"E10.sketch_text.stroke-64"),sQuery(id+"F4.wireOp",EDGE,"E10.sketch_text.stroke-65"),sQuery(id+"F4.wireOp",EDGE,"E10.sketch_text.stroke-66"),sQuery(id+"F4.wireOp",EDGE,"E10.sketch_text.stroke-67"),sQuery(id+"F4.wireOp",EDGE,"E10.sketch_text.stroke-68"),sQuery(id+"F4.wireOp",EDGE,"E10.sketch_text.stroke-69"),sQuery(id+"F4.wireOp",EDGE,"E10.sketch_text.stroke-70"),sQuery(id+"F4.wireOp",EDGE,"E10.sketch_text.stroke-71"),sQuery(id+"F4.wireOp",EDGE,"E10.sketch_text.stroke-72"),sQuery(id+"F4.wireOp",EDGE,"E10.sketch_text.stroke-73"),sQuery(id+"F4.wireOp",EDGE,"E10.sketch_text.stroke-74"),sQuery(id+"F4.wireOp",EDGE,"E10.sketch_text.stroke-75"),sQuery(id+"F4.wireOp",EDGE,"E10.sketch_text.stroke-76"),sQuery(id+"F4.wireOp",EDGE,"E10.sketch_text.stroke-77"),sQuery(id+"F4.wireOp",EDGE,"E10.sketch_text.stroke-78"),sQuery(id+"F4.wireOp",EDGE,"E10.sketch_text.stroke-79"),sQuery(id+"F4.wireOp",EDGE,"E10.sketch_text.stroke-80"),sQuery(id+"F4.wireOp",EDGE,"E10.sketch_text.stroke-81"),sQuery(id+"F4.wireOp",EDGE,"E10.sketch_text.stroke-82"),sQuery(id+"F4.wireOp",EDGE,"E10.sketch_text.stroke-83"),sQuery(id+"F4.wireOp",EDGE,"E10.sketch_text.stroke-84"),sQuery(id+"F4.wireOp",EDGE,"E10.sketch_text.stroke-85"),sQuery(id+"F4.wireOp",EDGE,"E10.sketch_text.stroke-86"),sQuery(id+"F4.wireOp",EDGE,"E10.sketch_text.stroke-87"),sQuery(id+"F4.wireOp",EDGE,"E10.sketch_text.stroke-88"),sQuery(id+"F4.wireOp",EDGE,"E10.sketch_text.stroke-89"),sQuery(id+"F4.wireOp",EDGE,"E10.sketch_text.stroke-90"),sQuery(id+"F4.wireOp",EDGE,"E10.sketch_text.stroke-91"),sQuery(id+"F4.wireOp",EDGE,"E10.sketch_text.stroke-92"),sQuery(id+"F4.wireOp",EDGE,"E10.sketch_text.stroke-93"),sQuery(id+"F4.wireOp",EDGE,"E10.sketch_text.stroke-94"),sQuery(id+"F4.wireOp",EDGE,"E10.sketch_text.stroke-95"),sQuery(id+"F4.wireOp",EDGE,"E10.sketch_text.stroke-96"),sQuery(id+"F4.wireOp",EDGE,"E10.sketch_text.stroke-97"),sQuery(id+"F4.wireOp",EDGE,"E10.sketch_text.stroke-98"),sQuery(id+"F4.wireOp",EDGE,"E10.sketch_text.stroke-99"),sQuery(id+"F4.wireOp",EDGE,"E10.sketch_text.stroke-100"),sQuery(id+"F4.wireOp",EDGE,"E10.sketch_text.stroke-101"),sQuery(id+"F4.wireOp",EDGE,"E10.sketch_text.stroke-102"),sQuery(id+"F4.wireOp",EDGE,"E10.sketch_text.stroke-103"),sQuery(id+"F4.wireOp",EDGE,"E10.sketch_text.stroke-104")])],"isStart":false});
            var Q117;
            Q117=makeQuery(id+"F5.opExtrude","SWEPT_FACE",FACE,{"disambiguationData":[OSD([sQuery(id+"F4.wireOp",EDGE,"E10.sketch_text.stroke-33")])]});
            var Q118;
            Q118=makeQuery(id+"F5.opExtrude","SWEPT_FACE",FACE,{"disambiguationData":[OSD([sQuery(id+"F4.wireOp",EDGE,"E10.sketch_text.stroke-93")])]});
            var Q119;
            Q119=makeQuery(id+"F5.opExtrude","SWEPT_FACE",FACE,{"disambiguationData":[OSD([sQuery(id+"F4.wireOp",EDGE,"E10.sketch_text.stroke-34")])]});
            var Q120;
            Q120=makeQuery(id+"F5.opExtrude","SWEPT_FACE",FACE,{"disambiguationData":[OSD([sQuery(id+"F4.wireOp",EDGE,"E10.sketch_text.stroke-152")])]});
            var Q121;
            Q121=makeQuery(id+"F5.opExtrude","SWEPT_FACE",FACE,{"disambiguationData":[OSD([sQuery(id+"F4.wireOp",EDGE,"E10.sketch_text.stroke-51")])]});
            var Q122;
            Q122=makeQuery(id+"F5.opExtrude","SWEPT_FACE",FACE,{"disambiguationData":[OSD([sQuery(id+"F4.wireOp",EDGE,"E10.sketch_text.stroke-6")])]});
            var Q123;
            Q123=makeQuery(id+"F5.opExtrude","SWEPT_FACE",FACE,{"disambiguationData":[OSD([sQuery(id+"F4.wireOp",EDGE,"E10.sketch_text.stroke-7")])]});
            var Q124;
            Q124=makeQuery(id+"F5.opExtrude","SWEPT_FACE",FACE,{"disambiguationData":[OSD([sQuery(id+"F4.wireOp",EDGE,"E10.sketch_text.stroke-156")])]});
            var Q125;
            Q125=makeQuery(id+"F5.opExtrude","SWEPT_FACE",FACE,{"disambiguationData":[OSD([sQuery(id+"F4.wireOp",EDGE,"E10.sketch_text.stroke-112")])]});
            var Q126;
            Q126=makeQuery(id+"F5.boolean.opBoolean","SPLIT",FACE,{"disambiguationData":[TD([makeQuery(id+"F5.opExtrude","SWEPT_FACE",FACE,{"disambiguationData":[OSD([sQuery(id+"F4.wireOp",EDGE,"E10.sketch_text.stroke-182")])]})])],"derivedFrom":makeQuery(id+"F1.opExtrude","CAP_FACE",FACE,{"disambiguationData":[OSD([sQuery(id+"F0.wireOp",EDGE,"E0.bottom"),sQuery(id+"F0.wireOp",EDGE,"E0.top"),sQuery(id+"F0.wireOp",EDGE,"E0.left"),sQuery(id+"F0.wireOp",EDGE,"E0.right"),sQuery(id+"F0.wireOp",EDGE,"E1"),sQuery(id+"F0.wireOp",EDGE,"E7.MirrorC"),sQuery(id+"F0.wireOp",EDGE,"E8.MirrorC"),sQuery(id+"F0.wireOp",EDGE,"E9.MirrorC")])],"isStart":true})});
            var Q127;
            Q127=makeQuery(id+"F5.opExtrude","SWEPT_FACE",FACE,{"disambiguationData":[OSD([sQuery(id+"F4.wireOp",EDGE,"E10.sketch_text.stroke-96")])]});
            var Q128;
            Q128=makeQuery(id+"F5.opExtrude","SWEPT_FACE",FACE,{"disambiguationData":[OSD([sQuery(id+"F4.wireOp",EDGE,"E10.sketch_text.stroke-114")])]});
            var Q129;
            Q129=makeQuery(id+"F5.opExtrude","SWEPT_FACE",FACE,{"disambiguationData":[OSD([sQuery(id+"F4.wireOp",EDGE,"E10.sketch_text.stroke-39")])]});
            var Q130;
            Q130=makeQuery(id+"F5.opExtrude","SWEPT_FACE",FACE,{"disambiguationData":[OSD([sQuery(id+"F4.wireOp",EDGE,"E10.sketch_text.stroke-13")])]});
            var Q131;
            Q131=makeQuery(id+"F5.opExtrude","SWEPT_FACE",FACE,{"disambiguationData":[OSD([sQuery(id+"F4.wireOp",EDGE,"E10.sketch_text.stroke-115")])]});
            var Q132;
            Q132=makeQuery(id+"F5.opExtrude","SWEPT_FACE",FACE,{"disambiguationData":[OSD([sQuery(id+"F4.wireOp",EDGE,"E10.sketch_text.stroke-56")])]});
            var Q133;
            Q133=makeQuery(id+"F5.opExtrude","SWEPT_FACE",FACE,{"disambiguationData":[OSD([sQuery(id+"F4.wireOp",EDGE,"E10.sketch_text.stroke-144")])]});
            var Q134;
            Q134=makeQuery(id+"F5.opExtrude","SWEPT_FACE",FACE,{"disambiguationData":[OSD([sQuery(id+"F4.wireOp",EDGE,"E10.sketch_text.stroke-190")])]});
            var Q135;
            Q135=makeQuery(id+"F5.opExtrude","SWEPT_FACE",FACE,{"disambiguationData":[OSD([sQuery(id+"F4.wireOp",EDGE,"E10.sketch_text.stroke-116")])]});
            var Q136;
            Q136=makeQuery(id+"F5.opExtrude","SWEPT_FACE",FACE,{"disambiguationData":[OSD([sQuery(id+"F4.wireOp",EDGE,"E10.sketch_text.stroke-41")])]});
            var Q137;
            Q137=makeQuery(id+"F5.opExtrude","SWEPT_FACE",FACE,{"disambiguationData":[OSD([sQuery(id+"F4.wireOp",EDGE,"E10.sketch_text.stroke-161")])]});
            var Q138;
            Q138=makeQuery(id+"F5.opExtrude","SWEPT_FACE",FACE,{"disambiguationData":[OSD([sQuery(id+"F4.wireOp",EDGE,"E10.sketch_text.stroke-146")])]});
            var Q139;
            Q139=makeQuery(id+"F5.opExtrude","SWEPT_FACE",FACE,{"disambiguationData":[OSD([sQuery(id+"F4.wireOp",EDGE,"E10.sketch_text.stroke-58")])]});
            var Q140;
            Q140=makeQuery(id+"F5.opExtrude","SWEPT_FACE",FACE,{"disambiguationData":[OSD([sQuery(id+"F4.wireOp",EDGE,"E10.sketch_text.stroke-105")])]});
            var Q141;
            Q141=makeQuery(id+"F5.opExtrude","SWEPT_FACE",FACE,{"disambiguationData":[OSD([sQuery(id+"F4.wireOp",EDGE,"E10.sketch_text.stroke-177")])]});
            var Q142;
            Q142=makeQuery(id+"F5.opExtrude","SWEPT_FACE",FACE,{"disambiguationData":[OSD([sQuery(id+"F4.wireOp",EDGE,"E10.sketch_text.stroke-77")])]});
            var Q143;
            Q143=makeQuery(id+"F5.opExtrude","SWEPT_FACE",FACE,{"disambiguationData":[OSD([sQuery(id+"F4.wireOp",EDGE,"E10.sketch_text.stroke-138")])]});
            var Q144;
            Q144=makeQuery(id+"F5.opExtrude","SWEPT_FACE",FACE,{"disambiguationData":[OSD([sQuery(id+"F4.wireOp",EDGE,"E10.sketch_text.stroke-111")])]});
            var Q145;
            Q145=makeQuery(id+"F5.opExtrude","SWEPT_FACE",FACE,{"disambiguationData":[OSD([sQuery(id+"F4.wireOp",EDGE,"E10.sketch_text.stroke-53")])]});
            var Q146;
            Q146=makeQuery(id+"F5.opExtrude","SWEPT_FACE",FACE,{"disambiguationData":[OSD([sQuery(id+"F4.wireOp",EDGE,"E10.sketch_text.stroke-141")])]});
            var Q147;
            Q147=makeQuery(id+"F5.opExtrude","SWEPT_FACE",FACE,{"disambiguationData":[OSD([sQuery(id+"F4.wireOp",EDGE,"E10.sketch_text.stroke-157")])]});
            var Q148;
            Q148=makeQuery(id+"F5.opExtrude","SWEPT_FACE",FACE,{"disambiguationData":[OSD([sQuery(id+"F4.wireOp",EDGE,"E10.sketch_text.stroke-64")])]});
            var Q149;
            Q149=makeQuery(id+"F5.boolean.opBoolean","SPLIT",FACE,{"disambiguationData":[TD([makeQuery(id+"F5.opExtrude","SWEPT_FACE",FACE,{"disambiguationData":[OSD([sQuery(id+"F4.wireOp",EDGE,"E10.sketch_text.stroke-53")])]})])],"derivedFrom":makeQuery(id+"F1.opExtrude","CAP_FACE",FACE,{"disambiguationData":[OSD([sQuery(id+"F0.wireOp",EDGE,"E0.bottom"),sQuery(id+"F0.wireOp",EDGE,"E0.top"),sQuery(id+"F0.wireOp",EDGE,"E0.left"),sQuery(id+"F0.wireOp",EDGE,"E0.right"),sQuery(id+"F0.wireOp",EDGE,"E1"),sQuery(id+"F0.wireOp",EDGE,"E7.MirrorC"),sQuery(id+"F0.wireOp",EDGE,"E8.MirrorC"),sQuery(id+"F0.wireOp",EDGE,"E9.MirrorC")])],"isStart":true})});
            var Q150;
            Q150=makeQuery(id+"F5.opExtrude","SWEPT_FACE",FACE,{"disambiguationData":[OSD([sQuery(id+"F4.wireOp",EDGE,"E10.sketch_text.stroke-36")])]});
            var Q151;
            Q151=makeQuery(id+"F5.opExtrude","SWEPT_FACE",FACE,{"disambiguationData":[OSD([sQuery(id+"F4.wireOp",EDGE,"E10.sketch_text.stroke-22")])]});
            var Q152;
            Q152=makeQuery(id+"F5.boolean.opBoolean","SPLIT",FACE,{"disambiguationData":[TD([makeQuery(id+"F5.opExtrude","SWEPT_FACE",FACE,{"disambiguationData":[OSD([sQuery(id+"F4.wireOp",EDGE,"E10.sketch_text.stroke-119")])]})])],"derivedFrom":makeQuery(id+"F1.opExtrude","CAP_FACE",FACE,{"disambiguationData":[OSD([sQuery(id+"F0.wireOp",EDGE,"E0.bottom"),sQuery(id+"F0.wireOp",EDGE,"E0.top"),sQuery(id+"F0.wireOp",EDGE,"E0.left"),sQuery(id+"F0.wireOp",EDGE,"E0.right"),sQuery(id+"F0.wireOp",EDGE,"E1"),sQuery(id+"F0.wireOp",EDGE,"E7.MirrorC"),sQuery(id+"F0.wireOp",EDGE,"E8.MirrorC"),sQuery(id+"F0.wireOp",EDGE,"E9.MirrorC")])],"isStart":true})});
            var Q153;
            Q153=makeQuery(id+"F5.boolean.opBoolean","SPLIT",FACE,{"disambiguationData":[TD([makeQuery(id+"F5.opExtrude","SWEPT_FACE",FACE,{"disambiguationData":[OSD([sQuery(id+"F4.wireOp",EDGE,"E10.sketch_text.stroke-158")])]})])],"derivedFrom":makeQuery(id+"F1.opExtrude","CAP_FACE",FACE,{"disambiguationData":[OSD([sQuery(id+"F0.wireOp",EDGE,"E0.bottom"),sQuery(id+"F0.wireOp",EDGE,"E0.top"),sQuery(id+"F0.wireOp",EDGE,"E0.left"),sQuery(id+"F0.wireOp",EDGE,"E0.right"),sQuery(id+"F0.wireOp",EDGE,"E1"),sQuery(id+"F0.wireOp",EDGE,"E7.MirrorC"),sQuery(id+"F0.wireOp",EDGE,"E8.MirrorC"),sQuery(id+"F0.wireOp",EDGE,"E9.MirrorC")])],"isStart":true})});
            var Q154;
            Q154=makeQuery(id+"F5.opExtrude","SWEPT_FACE",FACE,{"disambiguationData":[OSD([sQuery(id+"F4.wireOp",EDGE,"E10.sketch_text.stroke-9")])]});
            var Q155;
            Q155=makeQuery(id+"F5.opExtrude","SWEPT_FACE",FACE,{"disambiguationData":[OSD([sQuery(id+"F4.wireOp",EDGE,"E10.sketch_text.stroke-167")])]});
            var Q156;
            Q156=makeQuery(id+"F5.opExtrude","SWEPT_FACE",FACE,{"disambiguationData":[OSD([sQuery(id+"F4.wireOp",EDGE,"E10.sketch_text.stroke-95")])]});
            var Q157;
            Q157=makeQuery(id+"F5.opExtrude","SWEPT_FACE",FACE,{"disambiguationData":[OSD([sQuery(id+"F4.wireOp",EDGE,"E10.sketch_text.stroke-184")])]});
            var Q158;
            Q158=makeQuery(id+"F5.opExtrude","SWEPT_FACE",FACE,{"disambiguationData":[OSD([sQuery(id+"F4.wireOp",EDGE,"E10.sketch_text.stroke-84")])]});
            var Q159;
            Q159=makeQuery(id+"F5.opExtrude","SWEPT_FACE",FACE,{"disambiguationData":[OSD([sQuery(id+"F4.wireOp",EDGE,"E10.sketch_text.stroke-68")])]});
            var Q160;
            Q160=makeQuery(id+"F5.opExtrude","SWEPT_FACE",FACE,{"disambiguationData":[OSD([sQuery(id+"F4.wireOp",EDGE,"E10.sketch_text.stroke-143")])]});
            var Q161;
            Q161=makeQuery(id+"F5.opExtrude","SWEPT_FACE",FACE,{"disambiguationData":[OSD([sQuery(id+"F4.wireOp",EDGE,"E10.sketch_text.stroke-189")])]});
            var Q162;
            Q162=makeQuery(id+"F5.opExtrude","CAP_FACE",FACE,{"disambiguationData":[OSD([sQuery(id+"F4.wireOp",EDGE,"E10.sketch_text.stroke-13"),sQuery(id+"F4.wireOp",EDGE,"E10.sketch_text.stroke-14"),sQuery(id+"F4.wireOp",EDGE,"E10.sketch_text.stroke-15"),sQuery(id+"F4.wireOp",EDGE,"E10.sketch_text.stroke-16"),sQuery(id+"F4.wireOp",EDGE,"E10.sketch_text.stroke-17"),sQuery(id+"F4.wireOp",EDGE,"E10.sketch_text.stroke-18"),sQuery(id+"F4.wireOp",EDGE,"E10.sketch_text.stroke-19"),sQuery(id+"F4.wireOp",EDGE,"E10.sketch_text.stroke-20")])],"isStart":false});
            var Q163;
            Q163=makeQuery(id+"F5.opExtrude","SWEPT_FACE",FACE,{"disambiguationData":[OSD([sQuery(id+"F4.wireOp",EDGE,"E10.sketch_text.stroke-57")])]});
            var Q164;
            Q164=makeQuery(id+"F5.opExtrude","SWEPT_FACE",FACE,{"disambiguationData":[OSD([sQuery(id+"F4.wireOp",EDGE,"E10.sketch_text.stroke-29")])]});
            var Q165;
            Q165=makeQuery(id+"F5.opExtrude","SWEPT_FACE",FACE,{"disambiguationData":[OSD([sQuery(id+"F4.wireOp",EDGE,"E10.sketch_text.stroke-60")])]});
            var Q166;
            Q166=makeQuery(id+"F5.opExtrude","SWEPT_FACE",FACE,{"disambiguationData":[OSD([sQuery(id+"F4.wireOp",EDGE,"E10.sketch_text.stroke-148")])]});
            var Q167;
            Q167=makeQuery(id+"F5.opExtrude","SWEPT_FACE",FACE,{"disambiguationData":[OSD([sQuery(id+"F4.wireOp",EDGE,"E10.sketch_text.stroke-75")])]});
            var Q168;
            Q168=makeQuery(id+"F5.opExtrude","SWEPT_FACE",FACE,{"disambiguationData":[OSD([sQuery(id+"F4.wireOp",EDGE,"E10.sketch_text.stroke-91")])]});
            var Q169;
            Q169=makeQuery(id+"F5.opExtrude","SWEPT_FACE",FACE,{"disambiguationData":[OSD([sQuery(id+"F4.wireOp",EDGE,"E10.sketch_text.stroke-78")])]});
            var Q170;
            Q170=makeQuery(id+"F5.opExtrude","SWEPT_FACE",FACE,{"disambiguationData":[OSD([sQuery(id+"F4.wireOp",EDGE,"E10.sketch_text.stroke-62")])]});
            var Q171;
            Q171=makeQuery(id+"F5.opExtrude","SWEPT_FACE",FACE,{"disambiguationData":[OSD([sQuery(id+"F4.wireOp",EDGE,"E10.sketch_text.stroke-182")])]});
            var Q172;
            Q172=makeQuery(id+"F5.opExtrude","SWEPT_FACE",FACE,{"disambiguationData":[OSD([sQuery(id+"F4.wireOp",EDGE,"E10.sketch_text.stroke-11")])]});
            var Q173;
            Q173=makeQuery(id+"F5.opExtrude","SWEPT_FACE",FACE,{"disambiguationData":[OSD([sQuery(id+"F4.wireOp",EDGE,"E10.sketch_text.stroke-97")])]});
            var Q174;
            Q174=makeQuery(id+"F5.opExtrude","SWEPT_FACE",FACE,{"disambiguationData":[OSD([sQuery(id+"F4.wireOp",EDGE,"E10.sketch_text.stroke-23")])]});
            var Q175;
            Q175=makeQuery(id+"F5.opExtrude","SWEPT_FACE",FACE,{"disambiguationData":[OSD([sQuery(id+"F4.wireOp",EDGE,"E10.sketch_text.stroke-80")])]});
            var Q176;
            Q176=makeQuery(id+"F5.boolean.opBoolean","SPLIT",FACE,{"disambiguationData":[TD([makeQuery(id+"F5.opExtrude","SWEPT_FACE",FACE,{"disambiguationData":[OSD([sQuery(id+"F4.wireOp",EDGE,"E10.sketch_text.stroke-99")])]})])],"derivedFrom":makeQuery(id+"F1.opExtrude","CAP_FACE",FACE,{"disambiguationData":[OSD([sQuery(id+"F0.wireOp",EDGE,"E0.bottom"),sQuery(id+"F0.wireOp",EDGE,"E0.top"),sQuery(id+"F0.wireOp",EDGE,"E0.left"),sQuery(id+"F0.wireOp",EDGE,"E0.right"),sQuery(id+"F0.wireOp",EDGE,"E1"),sQuery(id+"F0.wireOp",EDGE,"E7.MirrorC"),sQuery(id+"F0.wireOp",EDGE,"E8.MirrorC"),sQuery(id+"F0.wireOp",EDGE,"E9.MirrorC")])],"isStart":true})});
            var Q177;
            Q177=makeQuery(id+"F5.opExtrude","SWEPT_FACE",FACE,{"disambiguationData":[OSD([sQuery(id+"F4.wireOp",EDGE,"E10.sketch_text.stroke-168")])]});
            var Q178;
            Q178=makeQuery(id+"F5.opExtrude","SWEPT_FACE",FACE,{"disambiguationData":[OSD([sQuery(id+"F4.wireOp",EDGE,"E10.sketch_text.stroke-188")])]});
            var Q179;
            Q179=makeQuery(id+"F5.opExtrude","SWEPT_FACE",FACE,{"disambiguationData":[OSD([sQuery(id+"F4.wireOp",EDGE,"E10.sketch_text.stroke-129")])]});
            var Q180;
            Q180=makeQuery(id+"F5.opExtrude","SWEPT_FACE",FACE,{"disambiguationData":[OSD([sQuery(id+"F4.wireOp",EDGE,"E10.sketch_text.stroke-27")])]});
            var Q181;
            Q181=makeQuery(id+"F5.opExtrude","SWEPT_FACE",FACE,{"disambiguationData":[OSD([sQuery(id+"F4.wireOp",EDGE,"E10.sketch_text.stroke-175")])]});
            var Q182;
            Q182=makeQuery(id+"F5.opExtrude","SWEPT_FACE",FACE,{"disambiguationData":[OSD([sQuery(id+"F4.wireOp",EDGE,"E10.sketch_text.stroke-42")])]});
            var Q183;
            Q183=makeQuery(id+"F5.opExtrude","SWEPT_FACE",FACE,{"disambiguationData":[OSD([sQuery(id+"F4.wireOp",EDGE,"E10.sketch_text.stroke-118")])]});
            var Q184;
            Q184=makeQuery(id+"F5.opExtrude","SWEPT_FACE",FACE,{"disambiguationData":[OSD([sQuery(id+"F4.wireOp",EDGE,"E10.sketch_text.stroke-151")])]});
            var Q185;
            Q185=makeQuery(id+"F5.opExtrude","SWEPT_FACE",FACE,{"disambiguationData":[OSD([sQuery(id+"F4.wireOp",EDGE,"E10.sketch_text.stroke-137")])]});
            var Q186;
            Q186=makeQuery(id+"F5.opExtrude","SWEPT_FACE",FACE,{"disambiguationData":[OSD([sQuery(id+"F4.wireOp",EDGE,"E10.sketch_text.stroke-83")])]});
            var Q187;
            Q187=makeQuery(id+"F5.boolean.opBoolean","SPLIT",FACE,{"disambiguationData":[TD([makeQuery(id+"F5.opExtrude","SWEPT_FACE",FACE,{"disambiguationData":[OSD([sQuery(id+"F4.wireOp",EDGE,"E10.sketch_text.stroke-90")])]})])],"derivedFrom":makeQuery(id+"F1.opExtrude","CAP_FACE",FACE,{"disambiguationData":[OSD([sQuery(id+"F0.wireOp",EDGE,"E0.bottom"),sQuery(id+"F0.wireOp",EDGE,"E0.top"),sQuery(id+"F0.wireOp",EDGE,"E0.left"),sQuery(id+"F0.wireOp",EDGE,"E0.right"),sQuery(id+"F0.wireOp",EDGE,"E1"),sQuery(id+"F0.wireOp",EDGE,"E7.MirrorC"),sQuery(id+"F0.wireOp",EDGE,"E8.MirrorC"),sQuery(id+"F0.wireOp",EDGE,"E9.MirrorC")])],"isStart":true})});
            var Q188;
            Q188=makeQuery(id+"F5.opExtrude","SWEPT_FACE",FACE,{"disambiguationData":[OSD([sQuery(id+"F4.wireOp",EDGE,"E10.sketch_text.stroke-139")])]});
            var Q189;
            Q189=makeQuery(id+"F5.opExtrude","SWEPT_FACE",FACE,{"disambiguationData":[OSD([sQuery(id+"F4.wireOp",EDGE,"E10.sketch_text.stroke-70")])]});
            var Q190;
            Q190=makeQuery(id+"F5.opExtrude","SWEPT_FACE",FACE,{"disambiguationData":[OSD([sQuery(id+"F4.wireOp",EDGE,"E10.sketch_text.stroke-160")])]});
            var Q191;
            Q191=makeQuery(id+"F5.opExtrude","SWEPT_FACE",FACE,{"disambiguationData":[OSD([sQuery(id+"F4.wireOp",EDGE,"E10.sketch_text.stroke-71")])]});
            var Q192;
            Q192=makeQuery(id+"F5.opExtrude","SWEPT_FACE",FACE,{"disambiguationData":[OSD([sQuery(id+"F4.wireOp",EDGE,"E10.sketch_text.stroke-117")])]});
            var Q193;
            Q193=makeQuery(id+"F5.opExtrude","SWEPT_FACE",FACE,{"disambiguationData":[OSD([sQuery(id+"F4.wireOp",EDGE,"E10.sketch_text.stroke-147")])]});
            var Q194;
            Q194=makeQuery(id+"F5.opExtrude","SWEPT_FACE",FACE,{"disambiguationData":[OSD([sQuery(id+"F4.wireOp",EDGE,"E10.sketch_text.stroke-164")])]});
            var Q195;
            Q195=makeQuery(id+"F5.opExtrude","SWEPT_FACE",FACE,{"disambiguationData":[OSD([sQuery(id+"F4.wireOp",EDGE,"E10.sketch_text.stroke-61")])]});
            var Q196;
            Q196=makeQuery(id+"F5.opExtrude","SWEPT_FACE",FACE,{"disambiguationData":[OSD([sQuery(id+"F4.wireOp",EDGE,"E10.sketch_text.stroke-19")])]});
            var Q197;
            Q197=makeQuery(id+"F5.opExtrude","SWEPT_FACE",FACE,{"disambiguationData":[OSD([sQuery(id+"F4.wireOp",EDGE,"E10.sketch_text.stroke-35")])]});
            var Q198;
            Q198=makeQuery(id+"F5.opExtrude","SWEPT_FACE",FACE,{"disambiguationData":[OSD([sQuery(id+"F4.wireOp",EDGE,"E10.sketch_text.stroke-140")])]});
            var Q199;
            Q199=makeQuery(id+"F5.opExtrude","SWEPT_FACE",FACE,{"disambiguationData":[OSD([sQuery(id+"F4.wireOp",EDGE,"E10.sketch_text.stroke-20")])]});
            var Q200;
            Q200=makeQuery(id+"F5.opExtrude","SWEPT_FACE",FACE,{"disambiguationData":[OSD([sQuery(id+"F4.wireOp",EDGE,"E10.sketch_text.stroke-16")])]});
            var Q201;
            Q201=makeQuery(id+"F5.opExtrude","SWEPT_FACE",FACE,{"disambiguationData":[OSD([sQuery(id+"F4.wireOp",EDGE,"E10.sketch_text.stroke-18")])]});
            var Q202;
            Q202=makeQuery(id+"F5.opExtrude","SWEPT_FACE",FACE,{"disambiguationData":[OSD([sQuery(id+"F4.wireOp",EDGE,"E10.sketch_text.stroke-17")])]});
            var Q203;
            Q203=qCreatedBy(makeId("Right.planeOp"),FACE);
            mirror(context, id + "F6", {"operationType" : NewBodyOperationType.ADD, "entities" : qUnion([Q0]), "faces" : qUnion([Q1, Q2, Q3, Q4, Q5, Q6, Q7, Q8, Q9, Q10, Q11, Q12, Q13, Q14, Q15, Q16, Q17, Q18, Q19, Q20, Q21, Q22, Q23, Q24, Q25, Q26, Q27, Q28, Q29, Q30, Q31, Q32, Q33, Q34, Q35, Q36, Q37, Q38, Q39, Q40, Q41, Q42, Q43, Q44, Q45, Q46, Q47, Q48, Q49, Q50, Q51, Q52, Q53, Q54, Q55, Q56, Q57, Q58, Q59, Q60, Q61, Q62, Q63, Q64, Q65, Q66, Q67, Q68, Q69, Q70, Q71, Q72, Q73, Q74, Q75, Q76, Q77, Q78, Q79, Q80, Q81, Q82, Q83, Q84, Q85, Q86, Q87, Q88, Q89, Q90, Q91, Q92, Q93, Q94, Q95, Q96, Q97, Q98, Q99, Q100, Q101, Q102, Q103, Q104, Q105, Q106, Q107, Q108, Q109, Q110, Q111, Q112, Q113, Q114, Q115, Q116, Q117, Q118, Q119, Q120, Q121, Q122, Q123, Q124, Q125, Q126, Q127, Q128, Q129, Q130, Q131, Q132, Q133, Q134, Q135, Q136, Q137, Q138, Q139, Q140, Q141, Q142, Q143, Q144, Q145, Q146, Q147, Q148, Q149, Q150, Q151, Q152, Q153, Q154, Q155, Q156, Q157, Q158, Q159, Q160, Q161, Q162, Q163, Q164, Q165, Q166, Q167, Q168, Q169, Q170, Q171, Q172, Q173, Q174, Q175, Q176, Q177, Q178, Q179, Q180, Q181, Q182, Q183, Q184, Q185, Q186, Q187, Q188, Q189, Q190, Q191, Q192, Q193, Q194, Q195, Q196, Q197, Q198, Q199, Q200, Q201, Q202]), "mirrorPlane" : qUnion([Q203])});
        }
    });
